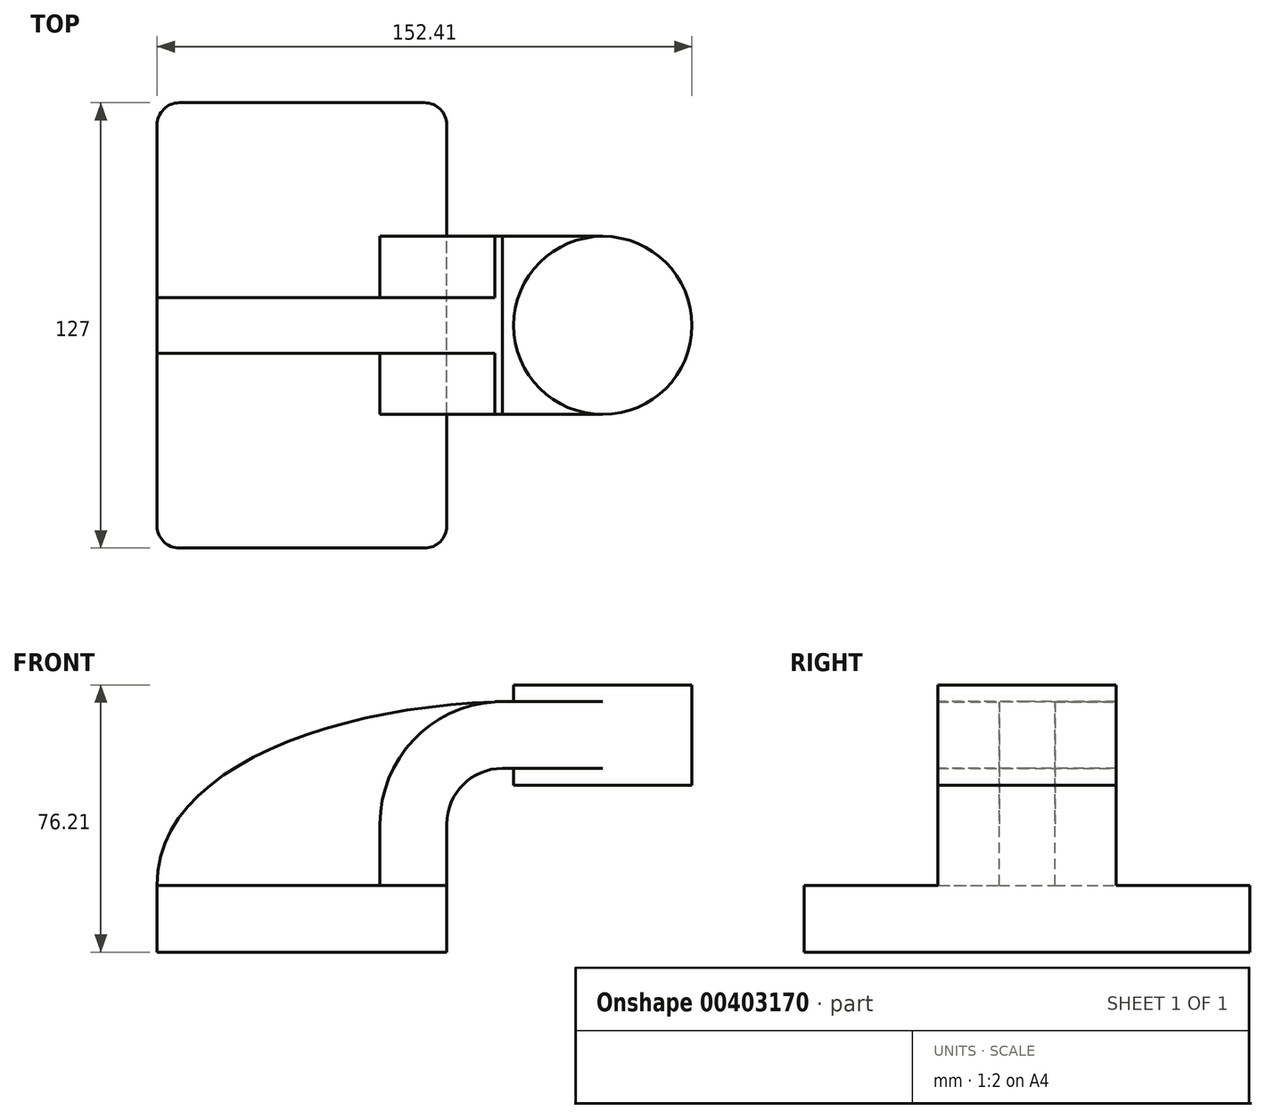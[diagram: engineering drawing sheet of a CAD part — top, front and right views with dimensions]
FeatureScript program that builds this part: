
annotation { "Feature Type Name" : "Feature", "Feature Type Description" : "" }
export const myFeature = defineFeature(function(context is Context, id is Id, definition is map)
    precondition{}
    {
        {
            var Q0;
            Q0=qCreatedBy(makeId("Front.planeOp"),FACE);
            var sketch = newSketch(context, id + "F0", { "sketchPlane" : qUnion([Q0])});
            skLineSegment(sketch, "E0.bottom", {"start": v(41.27, 9.53) * mm, "end": v(-41.28, 9.53) * mm});
            skLineSegment(sketch, "E0.top", {"start": v(41.28, -9.52) * mm, "end": v(-41.27, -9.52) * mm});
            skLineSegment(sketch, "E0.left", {"start": v(41.28, 9.53) * mm, "end": v(41.28, -9.52) * mm});
            skLineSegment(sketch, "E0.right", {"start": v(-41.28, 9.53) * mm, "end": v(-41.27, -9.52) * mm});
            skPoint(sketch, "E0.middle", {"position": v(0, 0) * mm});
            skLineSegment(sketch, "E1.bottom", {"start": v(111.12, 66.68) * mm, "end": v(60.32, 66.68) * mm});
            skLineSegment(sketch, "E1.top", {"start": v(111.12, 38.1) * mm, "end": v(60.32, 38.1) * mm});
            skLineSegment(sketch, "E1.left", {"start": v(111.12, 66.68) * mm, "end": v(111.12, 38.1) * mm});
            skLineSegment(sketch, "E1.right", {"start": v(60.32, 66.68) * mm, "end": v(60.32, 38.1) * mm});
            skPoint(sketch, "E1.middle", {"position": v(85.72, 52.39) * mm});
            skLineSegment(sketch, "E2", {"start": v(41.27, 9.53) * mm, "end": v(41.27, 27) * mm});
            skArc(sketch, "E3", {"start": v(41.27, 27) * mm, "mid": v(45.92, 38.23) * mm, "end": v(57.15, 42.88) * mm});
            skLineSegment(sketch, "E4", {"start": v(57.15, 42.88) * mm, "end": v(85.72, 42.88) * mm});
            skLineSegment(sketch, "E5.0", {"start": v(57.15, 61.93) * mm, "end": v(85.72, 61.93) * mm});
            skArc(sketch, "E5.1", {"start": v(22.23, 27) * mm, "mid": v(32.45, 51.7) * mm, "end": v(57.15, 61.93) * mm});
            skLineSegment(sketch, "E5.2", {"start": v(22.23, 9.53) * mm, "end": v(22.23, 27) * mm});
            skLineSegment(sketch, "E6", {"start": v(85.72, 38.1) * mm, "end": v(85.72, 66.68) * mm});
            skFitSpline(sketch, "E7", {"points": [v(-41.28, 9.53) * mm, v(57.15, 61.93) * mm], "startDerivative": vector(-1.5, 98.86) * mm, "endDerivative": vector(147.3, 3.93) * mm});
            skSolve(sketch);
        }
        {
            var Q0;
            Q0=makeQuery(id+"F0.imprint","IMPRINT",FACE,{"disambiguationData":[TD([[makeQuery(id+"F0.imprint","IMPRINT",EDGE,{"derivedFrom":sQuery(id+"F0.wireOp",EDGE,"E0.top")}),-1.0]])]});
            extrude(context, id + "F1", {"entities" : qUnion([Q0]), "endBound" : BoundingType.SYMMETRIC, "depth" : 127 * mm});
        }
        {
            var Q0;
            {var subQ3=sQuery(id+"F0.wireOp",EDGE,"E5.2");Q0=makeQuery(id+"F0.imprint","IMPRINT",FACE,{"disambiguationData":[TD([[makeQuery(id+"F0.imprint","IMPRINT",EDGE,{"derivedFrom":subQ3}),1.0]])]});}
            extrude(context, id + "F2", {"entities" : qUnion([Q0]), "operationType" : NewBodyOperationType.ADD, "endBound" : BoundingType.SYMMETRIC, "depth" : 15.88 * mm});
        }
        {
            var Q0;
            {var subQ1=sQuery(id+"F0.wireOp",EDGE,"E2");Q0=makeQuery(id+"F0.imprint","IMPRINT",FACE,{"disambiguationData":[TD([[makeQuery(id+"F0.imprint","IMPRINT",EDGE,{"derivedFrom":subQ1}),1.0]])]});}
            var Q1;
            {var subQ0=sQuery(id+"F0.wireOp",EDGE,"E5.0");var subQ1=sQuery(id+"F0.wireOp",EDGE,"E1.right");var subQ2=makeQuery(id+"F0.imprint","INTERSECT",VERTEX,{"derivedFrom":[subQ1,subQ0]});Q1=makeQuery(id+"F0.imprint","IMPRINT",FACE,{"disambiguationData":[TD([[makeQuery(id+"F0.imprint","IMPRINT",EDGE,{"disambiguationData":[TD([[subQ2,-1.0]])],"derivedFrom":subQ1}),1.0]])]});}
            extrude(context, id + "F3", {"entities" : qUnion([Q0, Q1]), "operationType" : NewBodyOperationType.ADD, "endBound" : BoundingType.SYMMETRIC, "depth" : 50.8 * mm});
        }
        {
            var Q0;
            {var subQ0=sQuery(id+"F0.wireOp",EDGE,"E1.left");Q0=makeQuery(id+"F0.imprint","IMPRINT",FACE,{"disambiguationData":[TD([[makeQuery(id+"F0.imprint","IMPRINT",EDGE,{"derivedFrom":subQ0}),-1.0]])]});}
            var Q1;
            Q1=sQuery(id+"F0.wireOp",EDGE,"E6");
            revolve(context, id + "F4", {"operationType" : NewBodyOperationType.ADD, "entities" : qUnion([Q0]), "axis" : qUnion([Q1]), "revolveType" : RevolveType.FULL});
        }
        {
            var Q0;
            Q0=makeQuery(id+"F1.opExtrude","CAP_EDGE",EDGE,{"disambiguationData":[OSD([sQuery(id+"F0.wireOp",EDGE,"E0.left")])],"isStart":false});
            var Q1;
            Q1=makeQuery(id+"F1.opExtrude","CAP_EDGE",EDGE,{"disambiguationData":[OSD([sQuery(id+"F0.wireOp",EDGE,"E0.right")])],"isStart":false});
            var Q2;
            Q2=makeQuery(id+"F1.opExtrude","CAP_EDGE",EDGE,{"disambiguationData":[OSD([sQuery(id+"F0.wireOp",EDGE,"E0.right")])],"isStart":true});
            var Q3;
            Q3=makeQuery(id+"F1.opExtrude","CAP_EDGE",EDGE,{"disambiguationData":[OSD([sQuery(id+"F0.wireOp",EDGE,"E0.left")])],"isStart":true});
            fillet(context, id + "F5", {"entities" : qUnion([Q0, Q1, Q2, Q3]), "radius" : 6.35 * mm, "tangentPropagation" : true, "allowEdgeOverflow" : false});
        }
    });
